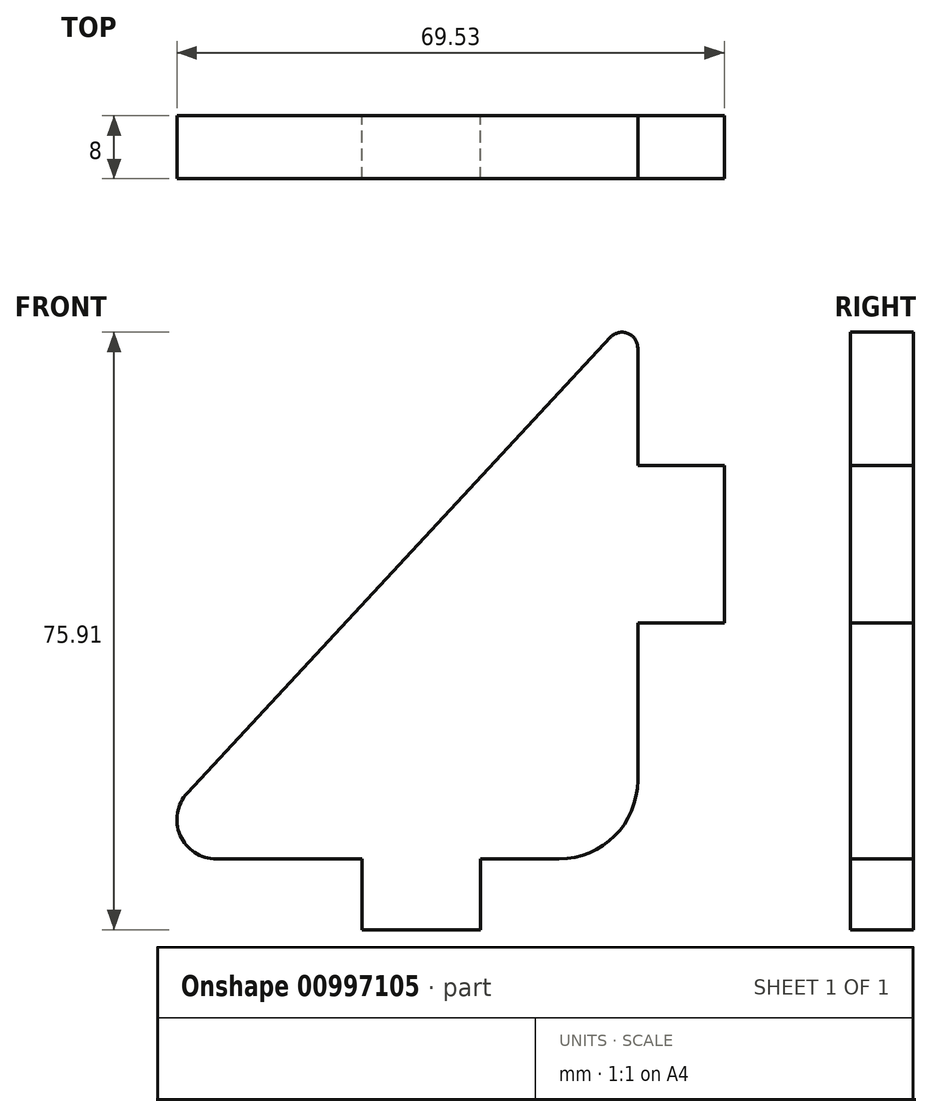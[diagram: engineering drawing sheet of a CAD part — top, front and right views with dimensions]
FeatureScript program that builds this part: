
annotation { "Feature Type Name" : "Feature", "Feature Type Description" : "" }
export const myFeature = defineFeature(function(context is Context, id is Id, definition is map)
    precondition{}
    {
        {
            var Q0;
            Q0=qCreatedBy(makeId("Front.planeOp"),FACE);
            var sketch = newSketch(context, id + "F0", { "sketchPlane" : qUnion([Q0])});
            skLineSegment(sketch, "E0", {"start": v(-53.53, 0) * mm, "end": v(-35, 0) * mm});
            skLineSegment(sketch, "E1", {"start": v(0, 10) * mm, "end": v(0, 30) * mm});
            skLineSegment(sketch, "E2", {"start": v(-3.47, 66.27) * mm, "end": v(-57.2, 8.4) * mm});
            skLineSegment(sketch, "E3", {"start": v(-35, 0) * mm, "end": v(-35, -9) * mm});
            skLineSegment(sketch, "E4", {"start": v(-35, -9) * mm, "end": v(-20, -9) * mm});
            skLineSegment(sketch, "E5", {"start": v(-20, -9) * mm, "end": v(-20, 0) * mm});
            skLineSegment(sketch, "E6", {"start": v(0, 30) * mm, "end": v(11, 30) * mm});
            skLineSegment(sketch, "E7", {"start": v(11, 30) * mm, "end": v(11, 50) * mm});
            skLineSegment(sketch, "E8", {"start": v(11, 50) * mm, "end": v(0, 50) * mm});
            skLineSegment(sketch, "E9.trimOffspring", {"start": v(-20, 0) * mm, "end": v(-10, 0) * mm});
            skLineSegment(sketch, "E10.trimOffspring", {"start": v(0, 50) * mm, "end": v(0, 64.9) * mm});
            skPoint(sketch, "E11.visualSharp", {"position": v(0, 70) * mm});
            skArc(sketch, "E11.filletArc", {"start": v(0, 64.9) * mm, "mid": v(-1.27, 66.77) * mm, "end": v(-3.47, 66.27) * mm});
            skPoint(sketch, "E12.visualSharp", {"position": v(-65, 0) * mm});
            skArc(sketch, "E12.filletArc", {"start": v(-57.2, 8.4) * mm, "mid": v(-58.12, 3) * mm, "end": v(-53.53, 0) * mm});
            skPoint(sketch, "E13.visualSharp", {"position": v(0, 0) * mm});
            skArc(sketch, "E13.filletArc", {"start": v(-10, 0) * mm, "mid": v(-2.93, 2.93) * mm, "end": v(0, 10) * mm});
            skSolve(sketch);
        }
        {
            var Q0;
            Q0 = qSketchRegion(id + "F0", true);
            extrude(context, id + "F1", {"entities" : qUnion([Q0]), "depth" : 8 * mm, "offsetDistance" : 25 * mm});
        }
    });
